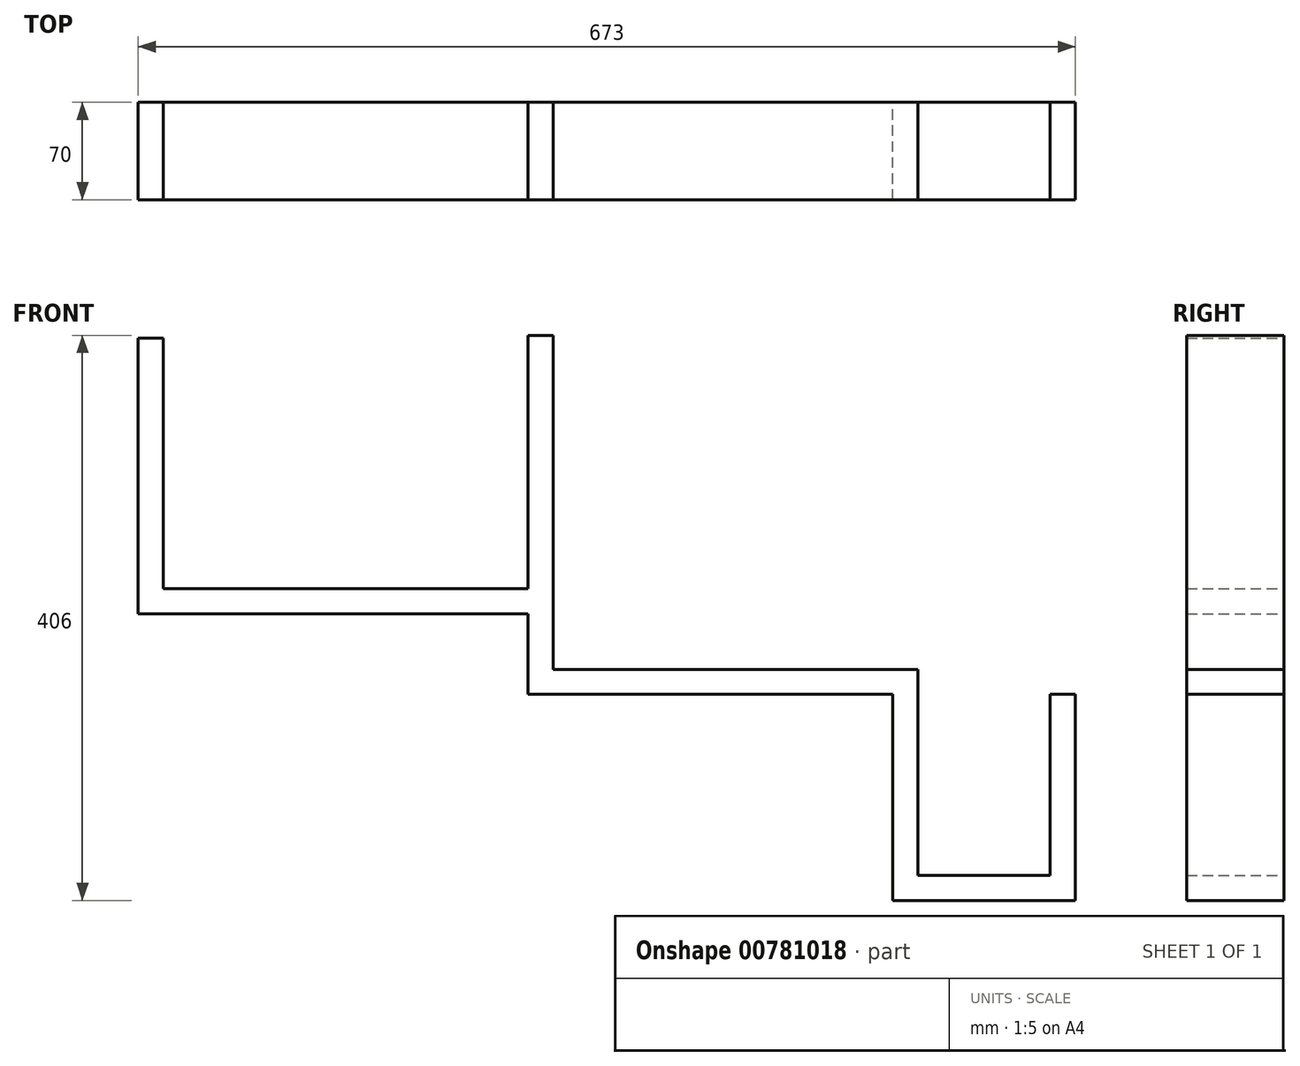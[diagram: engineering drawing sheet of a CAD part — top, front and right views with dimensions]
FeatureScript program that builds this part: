
annotation { "Feature Type Name" : "Feature", "Feature Type Description" : "" }
export const myFeature = defineFeature(function(context is Context, id is Id, definition is map)
    precondition{}
    {
        {
            var Q0;
            Q0=qCreatedBy(makeId("Front.planeOp"),FACE);
            var sketch = newSketch(context, id + "F0", { "sketchPlane" : qUnion([Q0])});
            skLineSegment(sketch, "E0.bottom", {"start": v(0, 0) * mm, "end": v(-18, 0) * mm});
            skLineSegment(sketch, "E0.top", {"start": v(0, 258) * mm, "end": v(-18, 258) * mm});
            skLineSegment(sketch, "E0.left", {"start": v(0, 0) * mm, "end": v(0, 258) * mm});
            skLineSegment(sketch, "E0.right", {"start": v(-18, 0) * mm, "end": v(-18, 258) * mm});
            skLineSegment(sketch, "E1.bottom", {"start": v(-18, 0) * mm, "end": v(262, 0) * mm});
            skLineSegment(sketch, "E1.top", {"start": v(-18, 18) * mm, "end": v(262, 18) * mm});
            skLineSegment(sketch, "E1.left", {"start": v(-18, 0) * mm, "end": v(-18, 18) * mm});
            skLineSegment(sketch, "E1.right", {"start": v(262, 0) * mm, "end": v(262, 18) * mm});
            skLineSegment(sketch, "E2.bottom", {"start": v(262, 0) * mm, "end": v(244, 0) * mm});
            skLineSegment(sketch, "E2.top", {"start": v(262, -130) * mm, "end": v(244, -130) * mm});
            skLineSegment(sketch, "E2.left", {"start": v(262, 0) * mm, "end": v(262, -130) * mm});
            skLineSegment(sketch, "E2.right", {"start": v(244, 0) * mm, "end": v(244, -130) * mm});
            skLineSegment(sketch, "E3.bottom", {"start": v(244, -130) * mm, "end": v(375, -130) * mm});
            skLineSegment(sketch, "E3.top", {"start": v(244, -148) * mm, "end": v(375, -148) * mm});
            skLineSegment(sketch, "E3.left", {"start": v(244, -130) * mm, "end": v(244, -148) * mm});
            skLineSegment(sketch, "E3.right", {"start": v(375, -130) * mm, "end": v(375, -148) * mm});
            skLineSegment(sketch, "E4.bottom", {"start": v(375, -148) * mm, "end": v(357, -148) * mm});
            skLineSegment(sketch, "E4.top", {"start": v(375, 0) * mm, "end": v(357, 0) * mm});
            skLineSegment(sketch, "E4.left", {"start": v(375, -148) * mm, "end": v(375, 0) * mm});
            skLineSegment(sketch, "E4.right", {"start": v(357, -148) * mm, "end": v(357, 0) * mm});
            skLineSegment(sketch, "E5", {"start": v(-18, 0) * mm, "end": v(-18, 66.82) * mm});
            skLineSegment(sketch, "E6", {"start": v(-18, 0) * mm, "end": v(-18, 58) * mm});
            skLineSegment(sketch, "E7.bottom", {"start": v(-18, 58) * mm, "end": v(-298, 58) * mm});
            skLineSegment(sketch, "E7.top", {"start": v(-18, 76) * mm, "end": v(-298, 76) * mm});
            skLineSegment(sketch, "E7.left", {"start": v(-18, 58) * mm, "end": v(-18, 76) * mm});
            skLineSegment(sketch, "E7.right", {"start": v(-298, 58) * mm, "end": v(-298, 76) * mm});
            skLineSegment(sketch, "E8.bottom", {"start": v(-298, 76) * mm, "end": v(-280, 76) * mm});
            skLineSegment(sketch, "E8.top", {"start": v(-298, 256) * mm, "end": v(-280, 256) * mm});
            skLineSegment(sketch, "E8.left", {"start": v(-298, 76) * mm, "end": v(-298, 256) * mm});
            skLineSegment(sketch, "E8.right", {"start": v(-280, 76) * mm, "end": v(-280, 256) * mm});
            skSolve(sketch);
        }
        {
            var Q0;
            Q0 = qSketchRegion(id + "F0", true);
            extrude(context, id + "F1", {"entities" : qUnion([Q0]), "depth" : 70 * mm, "offsetDistance" : 25 * mm});
        }
    });
